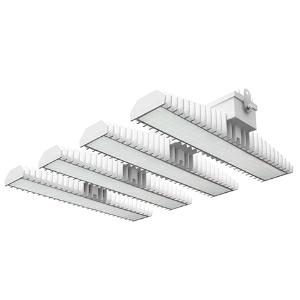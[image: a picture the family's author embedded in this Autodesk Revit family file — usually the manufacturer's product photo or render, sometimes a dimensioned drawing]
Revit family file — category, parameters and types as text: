
# Revit family: 3f_filippi_-_3f_lem_concentrato_3f_filippi_-_58890_a0812_-_3f_lem_4_led_200_cr_conc___vs_2797
name_source: partatom
category: Lighting Fixtures
units: mm (PartAtom-declared; Revit-internal decimal feet)

## family parameters
Cut with Voids When Loaded = No
Host = Face
Light Source = No
Part Type = Normal
Room Calculation Point = No
Round Connector Dimension = Use Diameter
Shared = No

## types (1)
- 3F Filippi - 3F LEM Concentrato (1 x LED, 26428 lm, 218 W, 4000 K)
    Apparent Load = 218 VA
    Approval mark = CE
    CIE Flux Codes = 78 93 98 100 100
    Color Rendering = 80
    Color Temperature = 4000 K
    Control Gear = Electronic ballast
    Default Elevation = 1800 mm
    Description = Industrial luminaire with high light output and high luminous efficiency designed with the most innovative technologies for environments with temperature up to 55°C.

ILLUMINOTECHNICAL
Luminous efficiency 100% (DLOR 98%, ULOR 2%).
Initial luminous flux of the luminaire 26428 lm.
Direct symmetric narrow distribution: the illuminated area has a elliptical shape.
Installation Interdistance Transv.D = 0.60 x hu - Long.D = 0.91 x hu.
Tabular UGR (CIE 117 - 4H-8H; S=0.25H; 70/50/20): RUG 20.2 - 21.8.
Beam angle: 38° - 61°.
Luminous efficacy 121 lm/W.
Lifetime (L93/B10): 30000 h. (tq+25°C)
Lifetime (L90/B10): 50000 h. (tq+25°C)
Lifetime (L85/B10): 80000 h. (tq+25°C)
Lifetime (L80/B10): 100000 h. (tq+25°C)
Lifetime (L85/B10): 50000 h. (tq+55°C)
Sudden decreased luminous flux after 50000 hours: 0% (C0).
Photobiological safety in compliance with IEC/TR 62778: RG0 risk exempt, (IEC 62471).
In compliance with IEC/EN 62722-2-1 - IEC/EN 62717 standards.

SOURCE
4 Mid-Power linear LED modules 50W/840.
Energy efficiency class (UE 2019/2020 - UE 2019/2015): C.
CIE 13.3 Colour rendering index: CRI >80 (R9 <50%).
IES TM-30 Fidelity Index: Rf = 84 Rg = 95.
CCT nominal colour temperature 4000 K.
Colour initial tolerance (MacAdam): SDCM 3.

MECHANICAL
Passive modular heatsinks in die-casted aluminium, painted in white colour.
To optimize the thermal management of the LED module, the heatsinks are oversized and provided with self-cleaning of cooling fins.
Wiring body in aluminium and galvanised steel anchored solidly to the sinks and thermally separated.
3F Lens lenses with high luminous efficiency, transparent methacrylate (PMMA), fixed to the LED modules.
Fixing brackets in stainless steel.
Luminaire with limited surface temperature. - D - (EN 60598-2-24)
Dimensions: 757x542 mm, height 133 mm. Weight 19.42 kg.
IP65 protection degree.
Mechanical strength to impacts IK06 (1 joule).
Glow-wire test resistance 650°C.

ELECTRICAL
Halogen Free electronic wiring 230V-50/60Hz, power factor 0.97, THD <25%, constant output current, class I, 2 driver.
Power of the luminaire 218 W.
ENEC - CE.
SAFE FLICKER: PstLM=<1 and SVM=<0.4 (IEC TR 61547-1 and IEC TR 63158), to ensure a more comfortable and safe light.
Luminaire compliant with EN 60598-2-22 for power supply from a centralised emergency system CPSS (Central Power Supply System), not incorporated in the luminaire - high risk areas excluded. The default power and flux are 100% in AC and 100% in DC.
Ambient temperature from -30°C to +55°C.
Temperature class T6 max 85°C.
Quick connection via M20 3P connector with 9-13 mm tightening range.
Power unit positioned on a separate compartment by the LED module to ensure optimum temperatures of cabling components, to be inspectable and maintainable.
Relative humidity UR: <85%.

INSTALLATION
Ceiling / Suspended / Wall.
All accessories dedicated to this product are available on the Catalog and on our website www.3F-Filippi.com.

ACCESSORIES
A0812 - Anti-glare microprismatic VS moulded glass, tempered, not flammable, with sealing gasket.
One required for each light module. The pack contains 10 pieces.

APPLICATIONS
In commercial environments, exhibition and industrial areas, stores, open areas or with shelves.
Applications with high ambient temperature up to 55°C.
Environments in which it is necessary a total protection against falling fragments (eg environments with foodstuffs or machines with moving parts or with extreme temperature changes), use luminaires with polycarbonate lenses.

WARNING
Fixture not suitable for cold stores with an ambient temperature <0°C and/or relative humidity >85%.
Luminaire designed for disposal/recycling at end-of-life.
Replaceable (LED only) light source by a professional. Replaceable control gear by a professional.
    Height = 133 mm  [stored 0.436352 ft]
    Lamp = 1 x LED
    Lamp Light Flux = 26428 lm
    Lamp Power = 218 W
    Lamp count = 1
    Length = 757 mm
    Lifetime = 50000 h
    Luminous efficacy = 121 lm/W
    Manufacturer = 3F Filippi
    ModVariant = No
    Model = 3F Filippi - 58890+A0812 - 3F LEM 4 LED 200 CR CONC + VS
    Mounting Place = Ceiling
    Mounting Type = Pendant
    Number of Poles = 1
    OnlyDefault = Yes
    Power Factor = 1
    Product Name = 3F Filippi - 3F LEM Concentrato
    Product group = pendant luminaire
    ProductGroupID = 9
    Protection Class = Protection class I
    Protection Degree = IP 65
    RLX_Detail_Level = 1
    RLX_Emergency_Light_Flux = 0 lm
    RLX_Emergency_Type = 0
    RLX_Emergency_Type_DB = No
    RlxData = <blob elided: 120669 chars, md5=90246ce9>
    Socket = socket
    Standby Power = 0 W
    System Light Flux = 26428 lm
    System Power = 218 W
    Type Comments = Product without accessories
    Type Image = 3f_filippi_-_lem_4__a0812.jpg
    URL = http://relux.com
    VarID = ---
    Voltage = 0 V
    Weight = 0.00 kg
    Width = 542 mm

note: [stored X ft] marks values corroborated as IEEE doubles in the binary element streams (Revit-internal decimal feet)

## geometry (parser evidence)
native form markers: Blend x4, Sweep x12
no freeform markers — native parametric forms only
